# Revit family: Valve_Box-Acudor-Surface_Mount-ASVB_Series
name_source: partatom
category: Specialty Equipment
revit_build: Autodesk Revit 2014 (Build: 20130308_1515(x64)
units: mm (PartAtom-declared; Revit-internal decimal feet)

## types (6) — shared parameters
Allen Head Cam Latch = No
Assembly Code = C1020700
Default Elevation = 48"
Description = Surface Mount Valve Boxes
Finish = Stainless Steel-Acudor-Type 304-Satin
Installation Type = Wall Mounted
Manufacturer = Acudor
Material = Stainless Steel-Acudor-Type-304-Satin
Product Documentation Link = https://www.acudor.com
Product Page URL = https://www.acudor.com
Recessed Non-Locking SS Paddle = No
Spanner Head Cam Latch = No
Stainless Steel Option = Yes
Steel Option = No
URL = http://acudor.com

## per-type parameters (varying)
| type | Height | Length | Width |
| ASVB 8x8x4 | 8" | 4" | 8" |
| ASVB 8x8x6 | 8" | 6" | 8" |
| ASVB 8x8x8 | 8" | 8" | 8" |
| ASVB 12x12x4 | 12" | 4" | 12" |
| ASVB 12x12x6 | 12" | 6" | 12" |
| ASVB 12x12x8 | 12" | 8" | 12" |

note: column(s) folded — value = type name in every type: Model

## geometry (parser evidence)
native form markers: Sweep x1
no freeform markers — native parametric forms only
